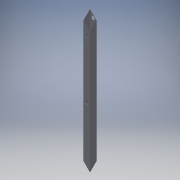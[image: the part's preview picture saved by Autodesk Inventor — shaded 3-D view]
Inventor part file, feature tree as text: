
AUTODESK INVENTOR PART (.ipt)
format: ipt  version: 2016 (Build 200138000, 138)  size: 120,832 bytes
history: native  units: in
note: dims shown in document units (in); Inventor stores cm internally (conversion verified against a paired STEP export)
features: extrude x4, sketch x4
ambient origin geometry x8: Origin, YZ Plane, XZ Plane, XY Plane, X Axis, Y Axis, Z Axis, Center Point
bodies: Solid1 (feature_tree)
feature tree (8):
  extrude  "Extrusion1"  Depth=1.0in
  extrude  "Extrusion2"  Depth=20.0in TaperAngle=0.0deg
  extrude  "Extrusion4"  Depth=1.0in
  extrude  "Extrusion5"  Depth=1.0in
  sketch  "Sketch1"  dims[d0=1.0in d1=1.0in]
  sketch  "Sketch2"  dims[d2=0.0625in d3=20.0in d4=0.0in]
  sketch  "Sketch4"  dims[d5=0.5in d6=1.0in]
  sketch  "Sketch5"  dims[d7=1.0in d8=0.0in d14=0.5in d15=0.456in d16=2.8in d17=1.0in d18=0.0in d19=0.5in d20=0.511in d21=8.694in d22=1.0in d23=0.0in]
